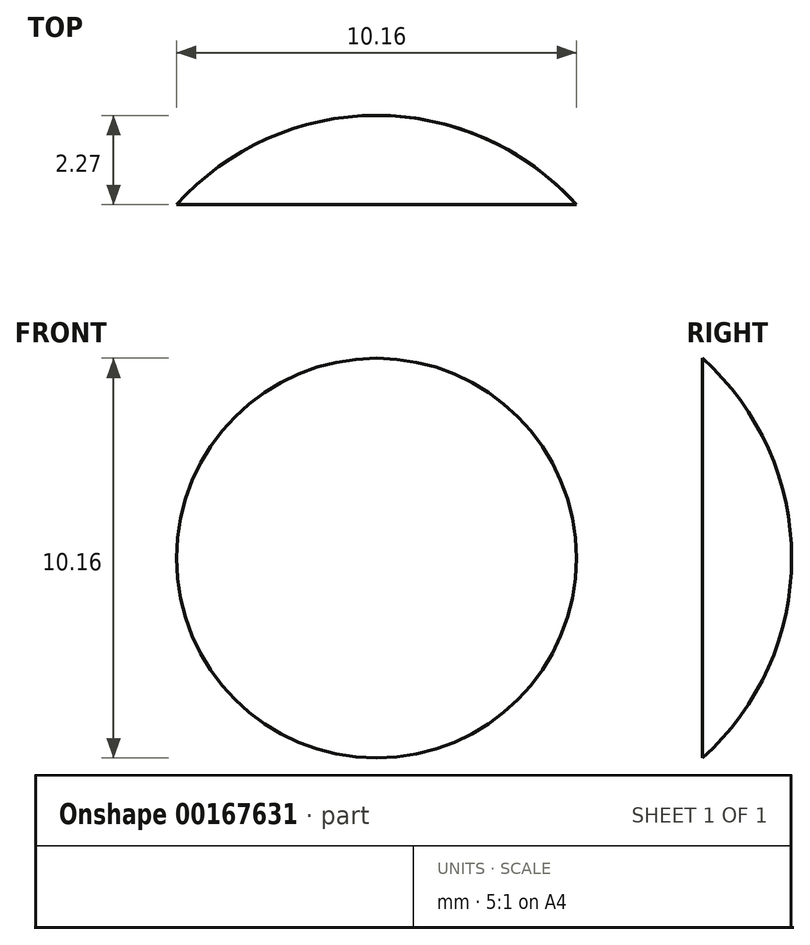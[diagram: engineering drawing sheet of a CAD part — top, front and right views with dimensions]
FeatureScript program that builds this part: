
annotation { "Feature Type Name" : "Feature", "Feature Type Description" : "" }
export const myFeature = defineFeature(function(context is Context, id is Id, definition is map)
    precondition{}
    {
        {
            var Q0;
            Q0=qCreatedBy(makeId("Top.planeOp"),FACE);
            var sketch = newSketch(context, id + "F0", { "sketchPlane" : qUnion([Q0])});
            skLineSegment(sketch, "E0", {"start": v(0, 0) * mm, "end": v(5.08, 0) * mm});
            skLineSegment(sketch, "E1", {"start": v(0, 0) * mm, "end": v(0, 2.27) * mm});
            skArc(sketch, "E2", {"start": v(5.08, 0) * mm, "mid": v(2.78, 1.68) * mm, "end": v(0, 2.27) * mm});
            skLineSegment(sketch, "E3.MirrorCS", {"start": v(0, 0) * mm, "end": v(-5.08, 0) * mm, "construction": true});
            skSolve(sketch);
        }
        {
            var Q0;
            Q0=makeQuery(id+"F0.imprint","IMPRINT",FACE,{"disambiguationData":[TD([[makeQuery(id+"F0.imprint","IMPRINT",EDGE,{"derivedFrom":sQuery(id+"F0.wireOp",EDGE,"E0")}),1.0]])]});
            var Q1;
            Q1=sQuery(id+"F0.wireOp",EDGE,"E1");
            revolve(context, id + "F1", {"entities" : qUnion([Q0]), "axis" : qUnion([Q1]), "revolveType" : RevolveType.FULL});
        }
    });
